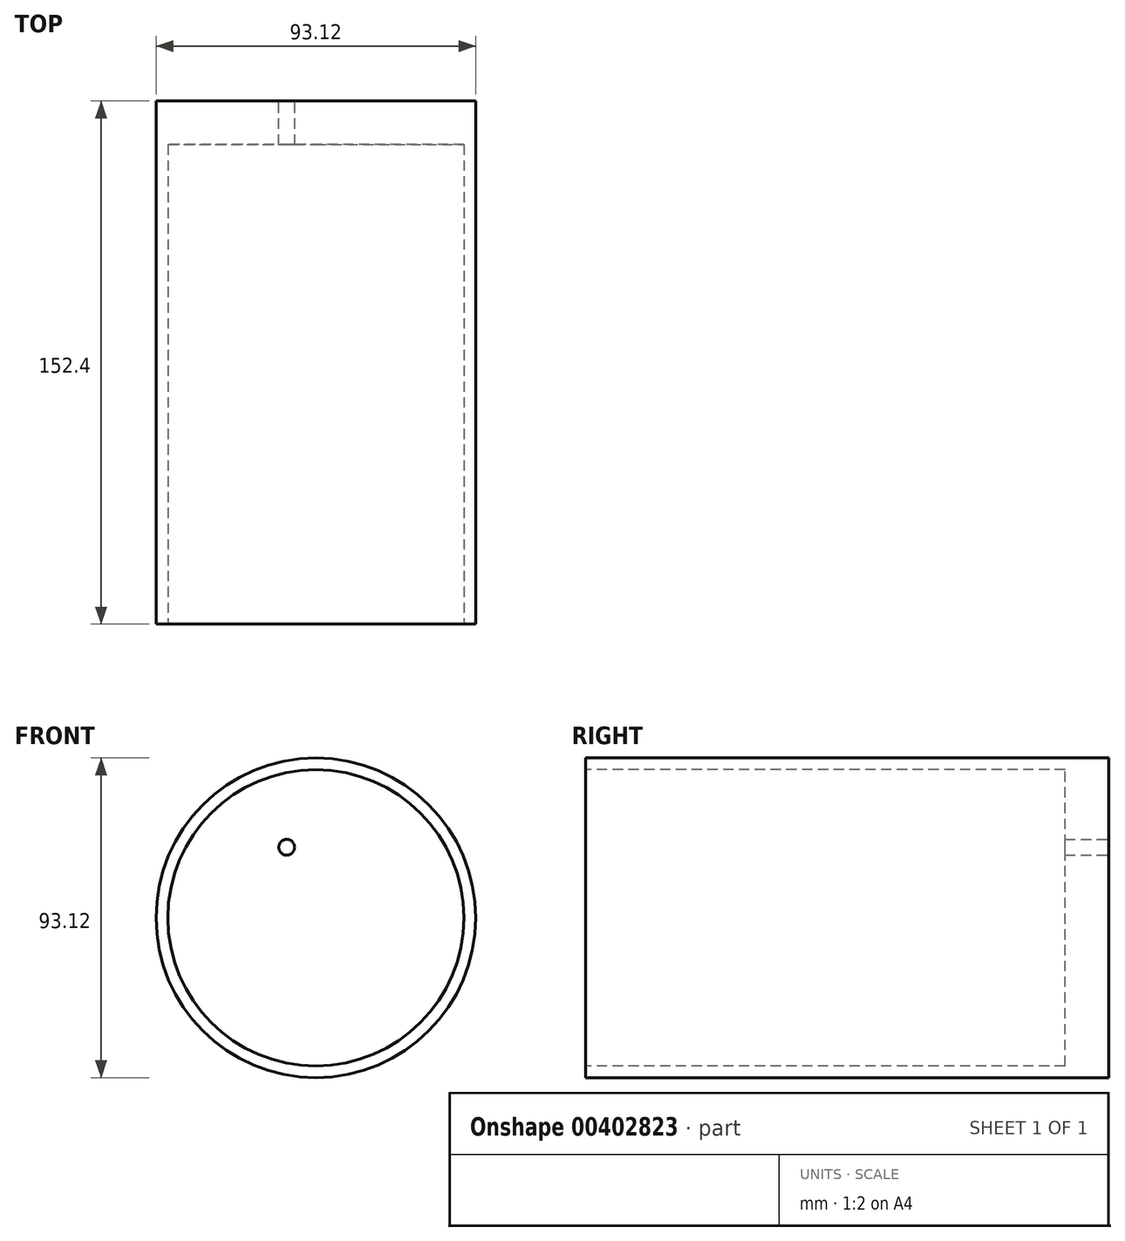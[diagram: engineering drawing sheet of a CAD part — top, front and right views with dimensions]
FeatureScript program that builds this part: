
annotation { "Feature Type Name" : "Feature", "Feature Type Description" : "" }
export const myFeature = defineFeature(function(context is Context, id is Id, definition is map)
    precondition{}
    {
        {
            var Q0;
            Q0=qCreatedBy(makeId("Front.planeOp"),FACE);
            var sketch = newSketch(context, id + "F0", { "sketchPlane" : qUnion([Q0])});
            skCircle(sketch, "E0", {"center": v(0, 0) * mm, "radius": 46.56 * mm});
            skCircle(sketch, "E1", {"center": v(-8.5, 20.53) * mm, "radius": 2.3 * mm});
            skSolve(sketch);
        }
        {
            var Q0;
            Q0=makeQuery(id+"F0.imprint","IMPRINT",FACE,{"disambiguationData":[TD([[makeQuery(id+"F0.imprint","IMPRINT",EDGE,{"derivedFrom":sQuery(id+"F0.wireOp",EDGE,"E0")}),1.0]])]});
            extrude(context, id + "F1", {"entities" : qUnion([Q0]), "depth" : 152.4 * mm});
        }
        {
            var Q0;
            Q0=makeQuery(id+"F1.opExtrude","CAP_FACE",FACE,{"disambiguationData":[OSD([sQuery(id+"F0.wireOp",EDGE,"E0"),sQuery(id+"F0.wireOp",EDGE,"E1")])],"isStart":false});
            var sketch = newSketch(context, id + "F2", { "sketchPlane" : qUnion([Q0])});
            skCircle(sketch, "E2", {"center": v(0, 0) * mm, "radius": 43.13 * mm});
            skSolve(sketch);
        }
        {
            var Q0;
            Q0 = qSketchRegion(id + "F2", true);
            extrude(context, id + "F3", {"entities" : qUnion([Q0]), "operationType" : NewBodyOperationType.REMOVE, "oppositeDirection" : true, "depth" : 139.7 * mm});
        }
    });
